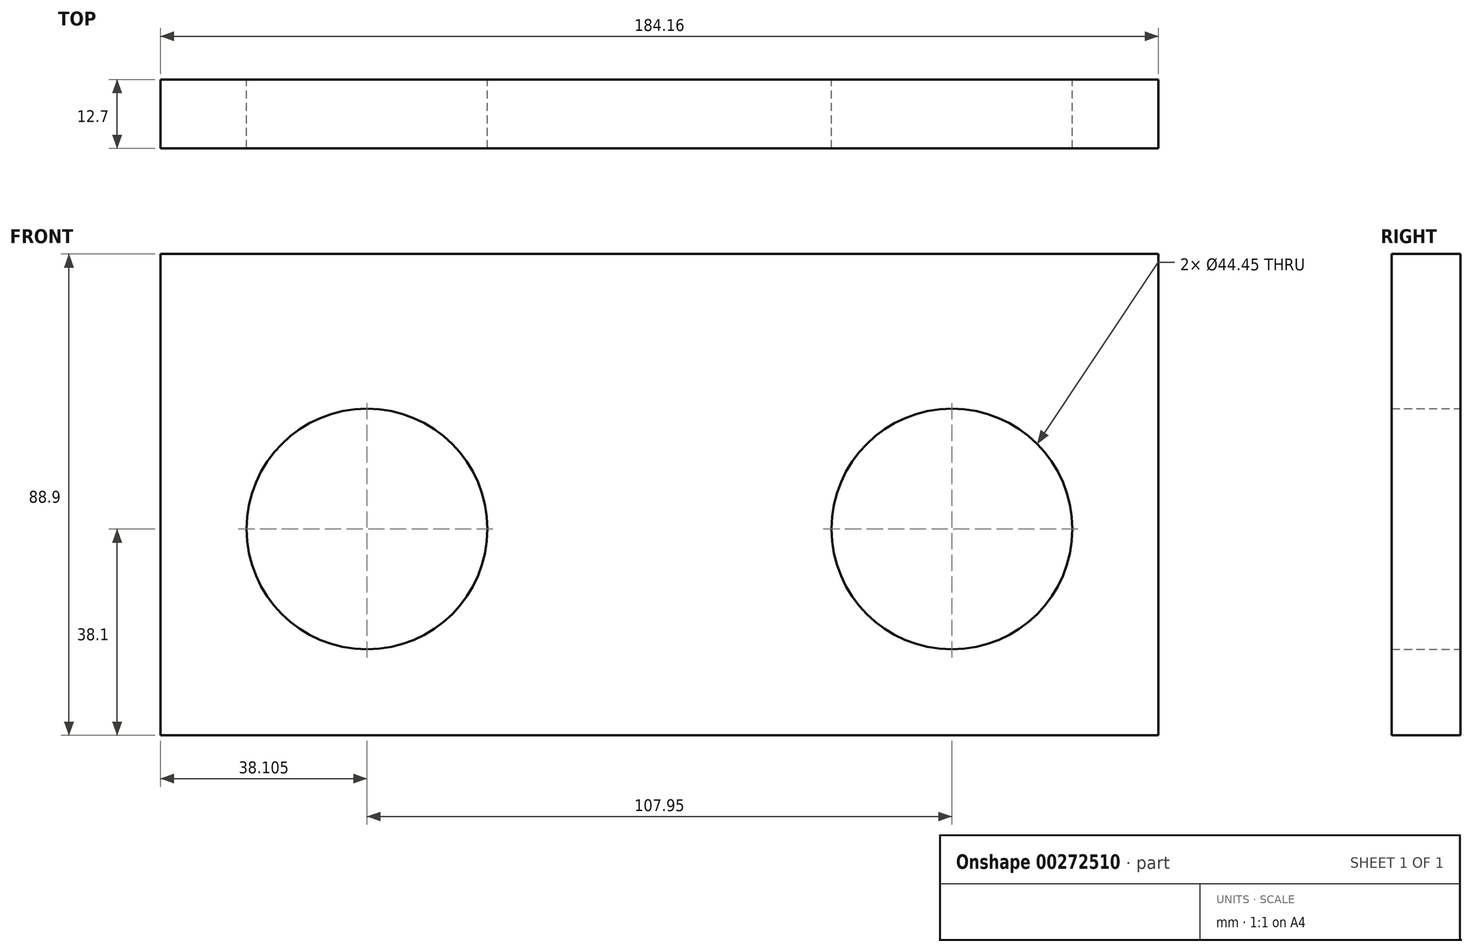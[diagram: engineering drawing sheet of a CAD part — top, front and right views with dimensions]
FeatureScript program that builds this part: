
annotation { "Feature Type Name" : "Feature", "Feature Type Description" : "" }
export const myFeature = defineFeature(function(context is Context, id is Id, definition is map)
    precondition{}
    {
        {
            var Q0;
            Q0=qCreatedBy(makeId("Front.planeOp"),FACE);
            var sketch = newSketch(context, id + "F0", { "sketchPlane" : qUnion([Q0])});
            skLineSegment(sketch, "E0.bottom", {"start": v(92.07, 44.45) * mm, "end": v(-92.07, 44.45) * mm});
            skLineSegment(sketch, "E0.top", {"start": v(92.08, -44.45) * mm, "end": v(-92.08, -44.45) * mm});
            skLineSegment(sketch, "E0.left", {"start": v(92.08, 44.45) * mm, "end": v(92.07, -44.45) * mm});
            skLineSegment(sketch, "E0.right", {"start": v(-92.07, 44.45) * mm, "end": v(-92.08, -44.45) * mm});
            skPoint(sketch, "E0.middle", {"position": v(0, 0) * mm});
            skLineSegment(sketch, "E1", {"start": v(0, -44.45) * mm, "end": v(0, -6.35) * mm});
            skPoint(sketch, "E1.endSnap0", {"position": v(0, -44.45) * mm});
            skLineSegment(sketch, "E2", {"start": v(-53.97, -6.35) * mm, "end": v(53.97, -6.35) * mm});
            skCircle(sketch, "E3", {"center": v(-53.97, -6.35) * mm, "radius": 22.23 * mm});
            skCircle(sketch, "E4", {"center": v(53.97, -6.35) * mm, "radius": 22.23 * mm});
            skLineSegment(sketch, "E5", {"start": v(0, 44.45) * mm, "end": v(0, 12.7) * mm});
            skPoint(sketch, "E5.endSnap0", {"position": v(0, 44.45) * mm});
            skLineSegment(sketch, "E6.bottom", {"start": v(-92.07, 44.45) * mm, "end": v(92.07, 44.45) * mm});
            skLineSegment(sketch, "E6.top", {"start": v(-92.07, 31.75) * mm, "end": v(92.07, 31.75) * mm});
            skLineSegment(sketch, "E6.left", {"start": v(-92.07, 44.45) * mm, "end": v(-92.07, 31.75) * mm});
            skLineSegment(sketch, "E6.right", {"start": v(92.08, 44.45) * mm, "end": v(92.08, 31.75) * mm});
            skLineSegment(sketch, "E7.top", {"start": v(92.07, -31.75) * mm, "end": v(-92.07, -31.75) * mm});
            skLineSegment(sketch, "E7.left", {"start": v(92.07, -44.45) * mm, "end": v(92.07, -31.75) * mm});
            skLineSegment(sketch, "E7.right", {"start": v(-92.08, -44.45) * mm, "end": v(-92.08, -31.75) * mm});
            skSolve(sketch);
        }
        {
            var Q0;
            Q0=qSketchRegion(id+"F0",true);
            extrude(context, id + "F1", {"entities" : qUnion([Q0]), "depth" : 12.7 * mm});
        }
    });
